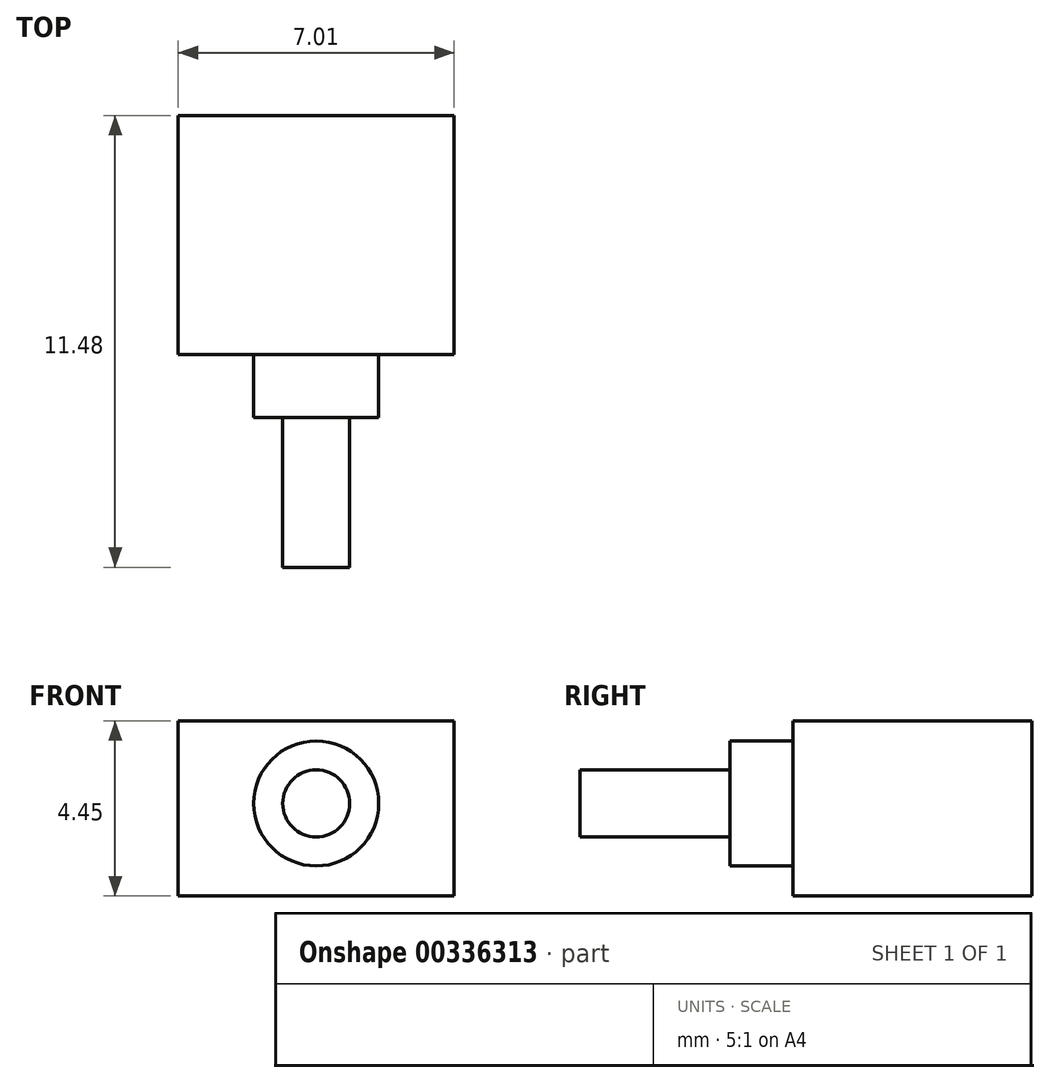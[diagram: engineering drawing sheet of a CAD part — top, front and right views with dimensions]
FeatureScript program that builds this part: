
annotation { "Feature Type Name" : "Feature", "Feature Type Description" : "" }
export const myFeature = defineFeature(function(context is Context, id is Id, definition is map)
    precondition{}
    {
        {
            var Q0;
            Q0=qCreatedBy(makeId("Front.planeOp"),FACE);
            var sketch = newSketch(context, id + "F0", { "sketchPlane" : qUnion([Q0])});
            skCircle(sketch, "E0", {"center": v(-12.78, 14.45) * mm, "radius": 0.85 * mm});
            skLineSegment(sketch, "E1.bottom", {"start": v(-9.28, 12.1) * mm, "end": v(-16.29, 12.1) * mm});
            skLineSegment(sketch, "E1.top", {"start": v(-9.28, 16.55) * mm, "end": v(-16.29, 16.55) * mm});
            skLineSegment(sketch, "E1.left", {"start": v(-9.28, 12.1) * mm, "end": v(-9.28, 16.55) * mm});
            skLineSegment(sketch, "E1.right", {"start": v(-16.29, 12.1) * mm, "end": v(-16.29, 16.55) * mm});
            skCircle(sketch, "E2", {"center": v(-12.78, 14.45) * mm, "radius": 1.59 * mm});
            skSolve(sketch);
        }
        {
            var Q0;
            Q0=makeQuery(id+"F0.imprint","IMPRINT",FACE,{"disambiguationData":[TD([[makeQuery(id+"F0.imprint","IMPRINT",EDGE,{"derivedFrom":sQuery(id+"F0.wireOp",EDGE,"E0")}),1.0]])]});
            extrude(context, id + "F1", {"entities" : qUnion([Q0]), "depth" : 5.4 * mm});
        }
        {
            var Q0;
            Q0=makeQuery(id+"F0.imprint","IMPRINT",FACE,{"disambiguationData":[TD([[makeQuery(id+"F0.imprint","IMPRINT",EDGE,{"derivedFrom":sQuery(id+"F0.wireOp",EDGE,"E0")}),-1.0]])]});
            var Q1;
            Q1=sQuery(id+"F0.wireOp",EDGE,"E2");
            extrude(context, id + "F2", {"entities" : qUnion([Q0]), "operationType" : NewBodyOperationType.ADD, "surfaceEntities" : qUnion([Q1]), "depth" : 1.6 * mm});
        }
        {
            var Q0;
            Q0 = qSketchRegion(id + "F0", true);
            var Q1;
            Q1=makeQuery(id+"F0.imprint","IMPRINT",FACE,{"disambiguationData":[TD([[makeQuery(id+"F0.imprint","IMPRINT",EDGE,{"derivedFrom":sQuery(id+"F0.wireOp",EDGE,"E0")}),-1.0]])]});
            var Q2;
            Q2=makeQuery(id+"F0.imprint","IMPRINT",FACE,{"disambiguationData":[TD([[makeQuery(id+"F0.imprint","IMPRINT",EDGE,{"derivedFrom":sQuery(id+"F0.wireOp",EDGE,"E0")}),1.0]])]});
            extrude(context, id + "F3", {"entities" : qUnion([Q0, Q1, Q2]), "depth" : -6.07 * mm});
        }
    });
